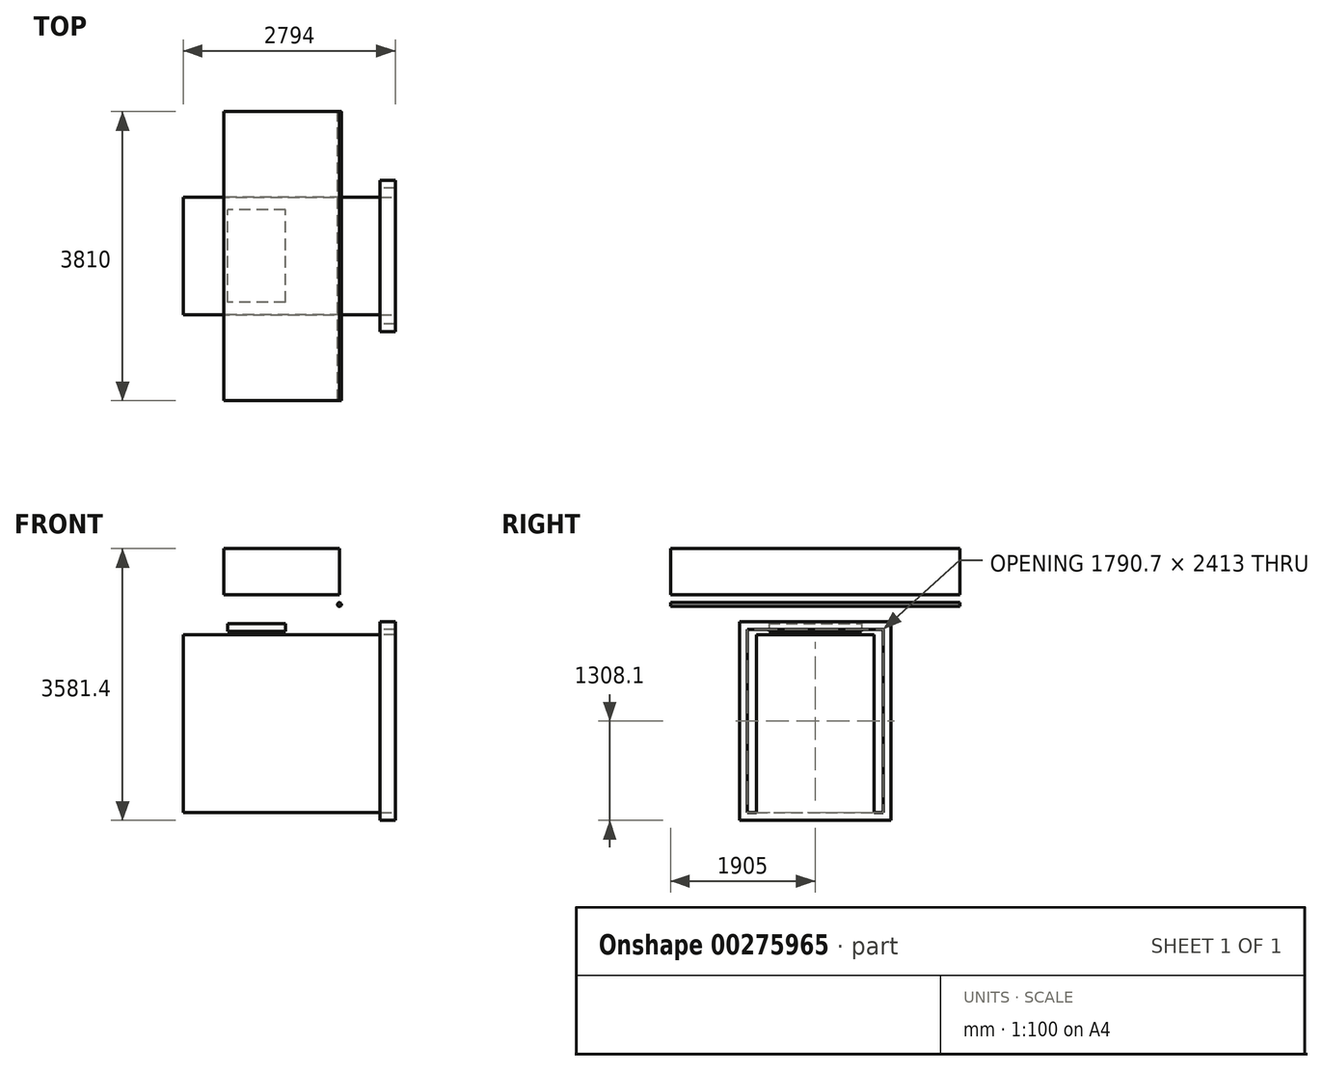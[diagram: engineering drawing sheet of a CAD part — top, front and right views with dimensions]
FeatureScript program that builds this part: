
annotation { "Feature Type Name" : "Feature", "Feature Type Description" : "" }
export const myFeature = defineFeature(function(context is Context, id is Id, definition is map)
    precondition{}
    {
        {
            var Q0;
            Q0=qCreatedBy(makeId("Right.planeOp"),FACE);
            var sketch = newSketch(context, id + "F0", { "sketchPlane" : qUnion([Q0])});
            skLineSegment(sketch, "E0.bottom", {"start": v(-895.35, 1206.5) * mm, "end": v(895.35, 1206.5) * mm});
            skLineSegment(sketch, "E0.top", {"start": v(-895.35, -1206.5) * mm, "end": v(895.35, -1206.5) * mm});
            skLineSegment(sketch, "E0.left", {"start": v(-895.35, 1206.5) * mm, "end": v(-895.35, -1206.5) * mm});
            skLineSegment(sketch, "E0.right", {"start": v(895.35, 1206.5) * mm, "end": v(895.35, -1206.5) * mm});
            skLineSegment(sketch, "E1.bottom", {"start": v(-996.95, 1308.1) * mm, "end": v(996.95, 1308.1) * mm});
            skLineSegment(sketch, "E1.top", {"start": v(-996.95, -1308.1) * mm, "end": v(996.95, -1308.1) * mm});
            skLineSegment(sketch, "E1.left", {"start": v(-996.95, 1308.1) * mm, "end": v(-996.95, -1308.1) * mm});
            skLineSegment(sketch, "E1.right", {"start": v(996.95, 1308.1) * mm, "end": v(996.95, -1308.1) * mm});
            skSolve(sketch);
        }
        {
            var Q0;
            Q0 = qSketchRegion(id + "F0", true);
            extrude(context, id + "F1", {"entities" : qUnion([Q0]), "depth" : 203.2 * mm});
        }
        {
            var Q0;
            Q0=makeQuery(id+"F1.opExtrude","CAP_FACE",FACE,{"disambiguationData":[OSD([sQuery(id+"F0.wireOp",EDGE,"E0.bottom"),sQuery(id+"F0.wireOp",EDGE,"E0.top"),sQuery(id+"F0.wireOp",EDGE,"E0.left"),sQuery(id+"F0.wireOp",EDGE,"E0.right"),sQuery(id+"F0.wireOp",EDGE,"E1.bottom"),sQuery(id+"F0.wireOp",EDGE,"E1.top"),sQuery(id+"F0.wireOp",EDGE,"E1.left"),sQuery(id+"F0.wireOp",EDGE,"E1.right")])],"isStart":true});
            cPlane(context, id + "F2", {"entities" : qUnion([Q0]), "cplaneType" : CPlaneType.OFFSET, "offset" : 533.4 * mm, "width" : 152.4 * mm, "height" : 152.4 * mm});
        }
        {
            var Q0;
            Q0=qCreatedBy(id+"F2.planeOp",FACE);
            var sketch = newSketch(context, id + "F3", { "sketchPlane" : qUnion([Q0])});
            skLineSegment(sketch, "E2.bottom", {"start": v(-1905, 2273.3) * mm, "end": v(1905, 2273.3) * mm});
            skLineSegment(sketch, "E2.top", {"start": v(-1905, 1663.7) * mm, "end": v(1905, 1663.7) * mm});
            skLineSegment(sketch, "E2.left", {"start": v(-1905, 2273.3) * mm, "end": v(-1905, 1663.7) * mm});
            skLineSegment(sketch, "E2.right", {"start": v(1905, 2273.3) * mm, "end": v(1905, 1663.7) * mm});
            skSolve(sketch);
        }
        {
            var Q0;
            Q0=makeQuery(id+"F3.imprint","IMPRINT",FACE,{"disambiguationData":[TD([[makeQuery(id+"F3.imprint","IMPRINT",EDGE,{"derivedFrom":sQuery(id+"F3.wireOp",EDGE,"E2.bottom")}),-1.0]])]});
            extrude(context, id + "F4", {"entities" : qUnion([Q0]), "depth" : 1524 * mm});
        }
        {
            var Q0;
            Q0=qCreatedBy(makeId("Front.planeOp"),FACE);
            var sketch = newSketch(context, id + "F5", { "sketchPlane" : qUnion([Q0])});
            skCircle(sketch, "E3", {"center": v(-533.4, 1536.7) * mm, "radius": 25.4 * mm});
            skSolve(sketch);
        }
        {
            var Q0;
            Q0=makeQuery(id+"F5.imprint","IMPRINT",FACE,{"disambiguationData":[TD([[makeQuery(id+"F5.imprint","IMPRINT",EDGE,{"derivedFrom":sQuery(id+"F5.wireOp",EDGE,"E3")}),1.0]])]});
            extrude(context, id + "F6", {"entities" : qUnion([Q0]), "depth" : 1905 * mm, "hasSecondDirection" : true, "secondDirectionOppositeDirection" : true, "secondDirectionDepth" : 1905 * mm});
        }
        {
            var Q0;
            Q0=qCreatedBy(makeId("Front.planeOp"),FACE);
            var sketch = newSketch(context, id + "F7", { "sketchPlane" : qUnion([Q0])});
            skLineSegment(sketch, "E4.bottom", {"start": v(-1244.6, 1282.7) * mm, "end": v(-2006.6, 1282.7) * mm});
            skLineSegment(sketch, "E4.top", {"start": v(-1244.6, 1181.1) * mm, "end": v(-2006.6, 1181.1) * mm});
            skLineSegment(sketch, "E4.left", {"start": v(-1244.6, 1282.7) * mm, "end": v(-1244.6, 1181.1) * mm});
            skLineSegment(sketch, "E4.right", {"start": v(-2006.6, 1282.7) * mm, "end": v(-2006.6, 1181.1) * mm});
            skSolve(sketch);
        }
        {
            var Q0;
            Q0=makeQuery(id+"F7.imprint","IMPRINT",FACE,{"disambiguationData":[TD([[makeQuery(id+"F7.imprint","IMPRINT",EDGE,{"derivedFrom":sQuery(id+"F7.wireOp",EDGE,"E4.bottom")}),1.0]])]});
            extrude(context, id + "F8", {"entities" : qUnion([Q0]), "depth" : 609.6 * mm, "hasSecondDirection" : true, "secondDirectionOppositeDirection" : true, "secondDirectionDepth" : 609.6 * mm});
        }
        {
            var Q0;
            Q0=qCreatedBy(makeId("Front.planeOp"),FACE);
            var sketch = newSketch(context, id + "F9", { "sketchPlane" : qUnion([Q0])});
            skPoint(sketch, "E5", {"position": v(203.2, 1139.19) * mm});
            skLineSegment(sketch, "E6", {"start": v(203.2, 1139.19) * mm, "end": v(-2590.8, 1139.19) * mm});
            skLineSegment(sketch, "E7", {"start": v(-2590.8, 1139.19) * mm, "end": v(-2590.8, -1206.5) * mm});
            skLineSegment(sketch, "E8", {"start": v(-2590.8, -1206.5) * mm, "end": v(203.2, -1206.5) * mm});
            skLineSegment(sketch, "E9", {"start": v(203.2, -1206.5) * mm, "end": v(203.2, 1139.19) * mm});
            skSolve(sketch);
        }
        {
            var Q0;
            Q0=makeQuery(id+"F9.imprint","IMPRINT",FACE,{"disambiguationData":[TD([[makeQuery(id+"F9.imprint","IMPRINT",EDGE,{"derivedFrom":sQuery(id+"F9.wireOp",EDGE,"E6")}),1.0]])]});
            extrude(context, id + "F10", {"entities" : qUnion([Q0]), "operationType" : NewBodyOperationType.ADD, "depth" : 774.7 * mm, "hasSecondDirection" : true, "secondDirectionOppositeDirection" : true, "secondDirectionDepth" : 774.7 * mm});
        }
    });
